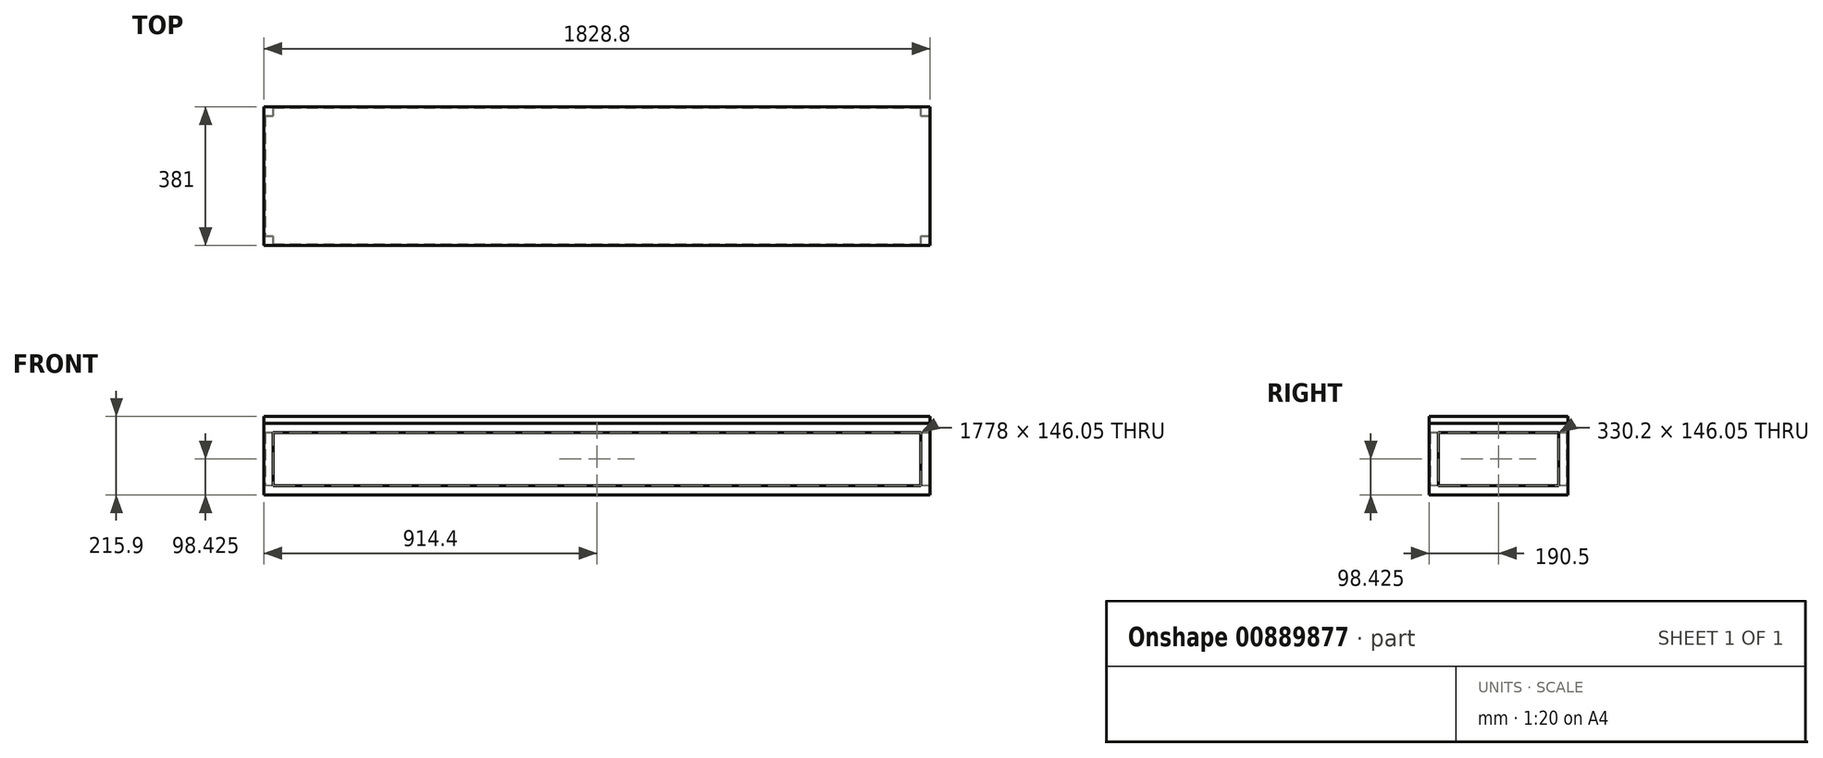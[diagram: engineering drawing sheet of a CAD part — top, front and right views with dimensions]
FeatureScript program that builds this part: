
annotation { "Feature Type Name" : "Feature", "Feature Type Description" : "" }
export const myFeature = defineFeature(function(context is Context, id is Id, definition is map)
    precondition{}
    {
        {
            var Q0;
            Q0=qCreatedBy(makeId("Top.planeOp"),FACE);
            var sketch = newSketch(context, id + "F0", { "sketchPlane" : qUnion([Q0])});
            skLineSegment(sketch, "E0.bottom", {"start": v(-914.4, 190.5) * mm, "end": v(914.4, 190.5) * mm});
            skLineSegment(sketch, "E0.top", {"start": v(-914.4, -190.5) * mm, "end": v(914.4, -190.5) * mm});
            skLineSegment(sketch, "E0.left", {"start": v(-914.4, 190.5) * mm, "end": v(-914.4, -190.5) * mm});
            skLineSegment(sketch, "E0.right", {"start": v(914.4, 190.5) * mm, "end": v(914.4, -190.5) * mm});
            skSolve(sketch);
        }
        {
            var Q0;
            Q0 = qSketchRegion(id + "F0", true);
            var Q1;
            Q1=sQuery(id+"F0.wireOp",EDGE,"E0.left");
            var Q2;
            Q2=sQuery(id+"F0.wireOp",EDGE,"E0.bottom");
            var Q3;
            Q3=sQuery(id+"F0.wireOp",EDGE,"E0.top");
            var Q4;
            Q4=sQuery(id+"F0.wireOp",EDGE,"E0.right");
            extrude(context, id + "F1", {"entities" : qUnion([Q0]), "surfaceEntities" : qUnion([Q1, Q2, Q3, Q4]), "depth" : 298.45 * mm, "offsetDistance" : 25.4 * mm});
        }
        {
            var Q0;
            Q0 = qSketchRegion(id + "F0", true);
            extrude(context, id + "F2", {"entities" : qUnion([Q0]), "operationType" : NewBodyOperationType.REMOVE, "depth" : 101.6 * mm, "offsetDistance" : 25.4 * mm});
        }
        {
            var Q0;
            Q0=makeQuery(id+"F1.opExtrude","CAP_FACE",FACE,{"disambiguationData":[OSD([sQuery(id+"F0.wireOp",EDGE,"E0.bottom"),sQuery(id+"F0.wireOp",EDGE,"E0.top"),sQuery(id+"F0.wireOp",EDGE,"E0.left"),sQuery(id+"F0.wireOp",EDGE,"E0.right")])],"isStart":false});
            var sketch = newSketch(context, id + "F3", { "sketchPlane" : qUnion([Q0])});
            skLineSegment(sketch, "E1.0", {"start": v(-914.4, 190.5) * mm, "end": v(914.4, 190.5) * mm});
            skLineSegment(sketch, "E2.0", {"start": v(-914.4, 190.5) * mm, "end": v(-914.4, -190.5) * mm});
            skLineSegment(sketch, "E3.0", {"start": v(-914.4, -190.5) * mm, "end": v(914.4, -190.5) * mm});
            skLineSegment(sketch, "E4.0", {"start": v(914.4, 190.5) * mm, "end": v(914.4, -190.5) * mm});
            skSolve(sketch);
        }
        {
            var Q0;
            Q0 = qSketchRegion(id + "F3", true);
            extrude(context, id + "F4", {"entities" : qUnion([Q0]), "depth" : 19.05 * mm, "offsetDistance" : 25.4 * mm});
        }
        {
            var Q0;
            Q0=makeQuery(id+"F1.opExtrude","SWEPT_FACE",FACE,{"disambiguationData":[OSD([sQuery(id+"F0.wireOp",EDGE,"E0.left")])]});
            var sketch = newSketch(context, id + "F5", { "sketchPlane" : qUnion([Q0])});
            skLineSegment(sketch, "E5.0", {"start": v(-165.1, 273.05) * mm, "end": v(-165.1, 127) * mm});
            skLineSegment(sketch, "E5.1", {"start": v(-165.1, 273.05) * mm, "end": v(165.1, 273.05) * mm});
            skLineSegment(sketch, "E5.2", {"start": v(165.1, 273.05) * mm, "end": v(165.1, 127) * mm});
            skLineSegment(sketch, "E5.3", {"start": v(-165.1, 127) * mm, "end": v(165.1, 127) * mm});
            skSolve(sketch);
        }
        {
            var Q0;
            Q0 = qSketchRegion(id + "F5", true);
            extrude(context, id + "F6", {"entities" : qUnion([Q0]), "operationType" : NewBodyOperationType.REMOVE, "endBound" : BoundingType.THROUGH_ALL, "oppositeDirection" : true, "depth" : 6.35 * mm, "offsetDistance" : 25.4 * mm});
        }
        {
            var Q0;
            Q0=makeQuery(id+"F1.opExtrude","SWEPT_FACE",FACE,{"disambiguationData":[OSD([sQuery(id+"F0.wireOp",EDGE,"E0.top")])]});
            var sketch = newSketch(context, id + "F7", { "sketchPlane" : qUnion([Q0])});
            skLineSegment(sketch, "E6.0", {"start": v(-889, 273.05) * mm, "end": v(-889, 127) * mm});
            skLineSegment(sketch, "E6.1", {"start": v(-889, 273.05) * mm, "end": v(889, 273.05) * mm});
            skLineSegment(sketch, "E6.2", {"start": v(889, 273.05) * mm, "end": v(889, 127) * mm});
            skLineSegment(sketch, "E6.3", {"start": v(-889, 127) * mm, "end": v(889, 127) * mm});
            skSolve(sketch);
        }
        {
            var Q0;
            Q0 = qSketchRegion(id + "F7", true);
            extrude(context, id + "F8", {"entities" : qUnion([Q0]), "operationType" : NewBodyOperationType.REMOVE, "endBound" : BoundingType.THROUGH_ALL, "oppositeDirection" : true, "depth" : 3.17 * mm, "offsetDistance" : 25.4 * mm});
        }
        {
            var Q0;
            Q0=makeQuery(id+"F8.boolean.opBoolean","MERGE",FACE,{"derivedFrom":[makeQuery(id+"F6.boolean.opBoolean","COPY",FACE,{"derivedFrom":makeQuery(id+"F6.opExtrude","SWEPT_FACE",FACE,{"disambiguationData":[OSD([sQuery(id+"F5.wireOp",EDGE,"E5.3")])]})})],"fromTools":[makeQuery(id+"F8.opExtrude","SWEPT_FACE",FACE,{"disambiguationData":[OSD([sQuery(id+"F7.wireOp",EDGE,"E6.3")])]})]});
            var sketch = newSketch(context, id + "F9", { "sketchPlane" : qUnion([Q0])});
            skLineSegment(sketch, "E7.0", {"start": v(-889, 165.1) * mm, "end": v(-911.23, 165.1) * mm});
            skLineSegment(sketch, "E8.0", {"start": v(-889, 187.32) * mm, "end": v(-889, 165.1) * mm});
            skLineSegment(sketch, "E9.0", {"start": v(-889, -165.1) * mm, "end": v(-889, -187.32) * mm});
            skLineSegment(sketch, "E10.0", {"start": v(-889, -165.1) * mm, "end": v(-911.23, -165.1) * mm});
            skLineSegment(sketch, "E11.0", {"start": v(911.23, 165.1) * mm, "end": v(889, 165.1) * mm});
            skLineSegment(sketch, "E12.0", {"start": v(889, 187.32) * mm, "end": v(889, 165.1) * mm});
            skLineSegment(sketch, "E13.0", {"start": v(911.23, -165.1) * mm, "end": v(889, -165.1) * mm});
            skLineSegment(sketch, "E14.0", {"start": v(889, -165.1) * mm, "end": v(889, -187.33) * mm});
            skLineSegment(sketch, "E15", {"start": v(889, -187.33) * mm, "end": v(-889, -187.32) * mm});
            skLineSegment(sketch, "E16", {"start": v(-911.23, -165.1) * mm, "end": v(-911.23, 165.1) * mm});
            skLineSegment(sketch, "E17.MirrorCS", {"start": v(911.23, -165.1) * mm, "end": v(911.23, 165.1) * mm});
            skLineSegment(sketch, "E18.MirrorCS", {"start": v(889, 187.33) * mm, "end": v(-889, 187.33) * mm});
            skPoint(sketch, "E19.orphan", {"position": v(-889, -190.5) * mm});
            skPoint(sketch, "E20.orphan", {"position": v(-914.4, -165.1) * mm});
            skPoint(sketch, "E21.orphan", {"position": v(-914.4, 165.1) * mm});
            skPoint(sketch, "E22.orphan", {"position": v(-889, 190.5) * mm});
            skPoint(sketch, "E23.orphan", {"position": v(889, -190.5) * mm});
            skPoint(sketch, "E24.orphan", {"position": v(914.4, -165.1) * mm});
            skPoint(sketch, "E25.orphan", {"position": v(914.4, 165.1) * mm});
            skPoint(sketch, "E26.orphan", {"position": v(889, 190.5) * mm});
            skSolve(sketch);
        }
        {
            var Q0;
            Q0 = qSketchRegion(id + "F9", true);
            var Q1;
            Q1=makeQuery(id+"F8.boolean.opBoolean","MERGE",FACE,{"derivedFrom":[makeQuery(id+"F6.boolean.opBoolean","COPY",FACE,{"derivedFrom":makeQuery(id+"F6.opExtrude","SWEPT_FACE",FACE,{"disambiguationData":[OSD([sQuery(id+"F5.wireOp",EDGE,"E5.1")])]})})],"fromTools":[makeQuery(id+"F8.opExtrude","SWEPT_FACE",FACE,{"disambiguationData":[OSD([sQuery(id+"F7.wireOp",EDGE,"E6.1")])]})]});
            extrude(context, id + "F10", {"entities" : qUnion([Q0]), "endBound" : BoundingType.UP_TO_SURFACE, "depth" : 25.4 * mm, "endBoundEntityFace" : qUnion([Q1]), "offsetDistance" : 25.4 * mm});
        }
    });
